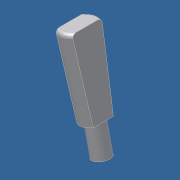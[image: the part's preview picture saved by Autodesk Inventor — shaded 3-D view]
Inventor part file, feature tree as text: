
AUTODESK INVENTOR PART (.ipt)
format: ipt  version: 2014 (Build 180170000, 170)  size: 107,008 bytes
history: native  units: in
note: dims shown in document units (in); Inventor stores cm internally (conversion verified against a paired STEP export)
features: other x14, sketch x2, revolve x1, extrude x1
ambient origin geometry x8: Origin, YZ Plane, XZ Plane, XY Plane, X Axis, Y Axis, Z Axis, Center Point
bodies: Solid1 (feature_tree)
feature tree (18):
  revolve  "Revolution1"  [1 undecoded]
  extrude  "Extrusion1"  [1 undecoded]
  other  "rot_XY"
  other  "rot_YZ"
  other  "rot_ZX"
  other  "rot_X"
  other  "rot_Y"
  other  "rot_Z"
  other  "rot_Center"
  other  "to_cap_XY"
  other  "to_cap_YZ"
  other  "to_cap_ZX"
  other  "to_cap_X"
  other  "to_cap_Y"
  other  "to_cap_Z"
  other  "to_cap_Center"
  sketch  "Sketch_4"  dims[d0=360.0deg d1=0.2in d2=0.0in]
  sketch  "Sketch_5"
note: 2 required parameter values undecoded (feature->parameter linkage not recoverable at this tier; creation-order binding heuristic only, values carry confidence <= 0.55)